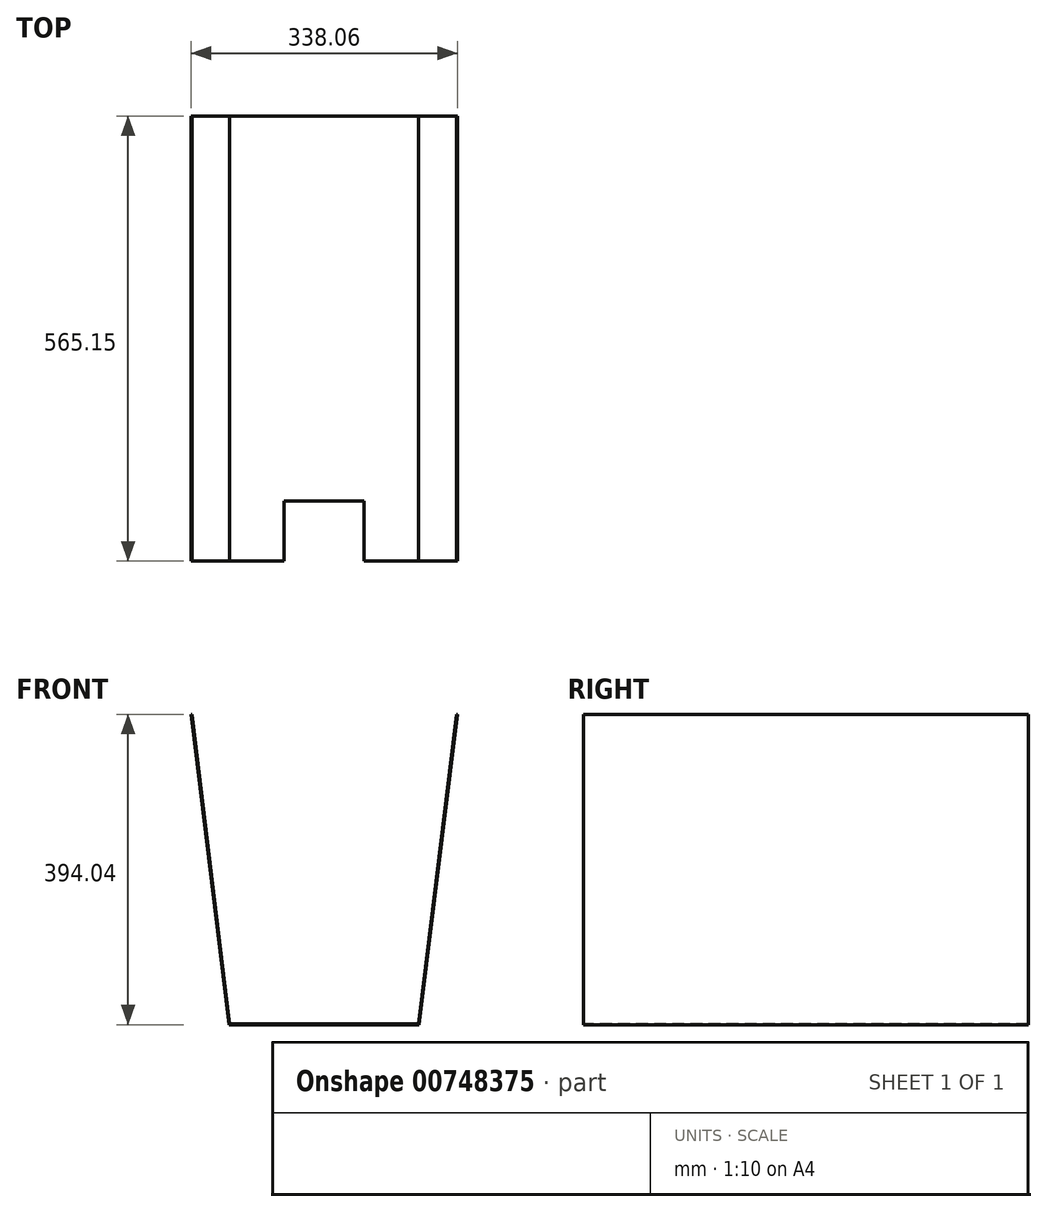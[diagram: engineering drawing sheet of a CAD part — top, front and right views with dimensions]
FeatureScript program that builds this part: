
annotation { "Feature Type Name" : "Feature", "Feature Type Description" : "" }
export const myFeature = defineFeature(function(context is Context, id is Id, definition is map)
    precondition{}
    {
        {
            var Q0;
            Q0=qCreatedBy(makeId("Front.planeOp"),FACE);
            var sketch = newSketch(context, id + "F0", { "sketchPlane" : qUnion([Q0])});
            skLineSegment(sketch, "E0", {"start": v(0, 0) * mm, "end": v(-120.65, 0) * mm});
            skLineSegment(sketch, "E1", {"start": v(-120.65, 0) * mm, "end": v(-169.03, 394.04) * mm});
            skLineSegment(sketch, "E2.MirrorCS", {"start": v(120.65, 0) * mm, "end": v(169.03, 394.04) * mm});
            skLineSegment(sketch, "E3.MirrorCS", {"start": v(0, 0) * mm, "end": v(120.65, 0) * mm});
            skLineSegment(sketch, "E4", {"start": v(-169.03, 394.04) * mm, "end": v(169.03, 394.04) * mm});
            skSolve(sketch);
        }
        {
            var Q0;
            Q0=makeQuery(id+"F0.imprint","IMPRINT",FACE,{"disambiguationData":[TD([[makeQuery(id+"F0.imprint","IMPRINT",EDGE,{"derivedFrom":sQuery(id+"F0.wireOp",EDGE,"E0")}),-1.0]])]});
            extrude(context, id + "F1", {"entities" : qUnion([Q0]), "depth" : -565.15 * mm, "offsetDistance" : 25.4 * mm});
        }
        {
            var Q0;
            Q0=makeQuery(id+"F1.opExtrude","CAP_FACE",FACE,{"disambiguationData":[OSD([sQuery(id+"F0.wireOp",EDGE,"E0"),sQuery(id+"F0.wireOp",EDGE,"E1"),sQuery(id+"F0.wireOp",EDGE,"E2.MirrorCS"),sQuery(id+"F0.wireOp",EDGE,"E3.MirrorCS"),sQuery(id+"F0.wireOp",EDGE,"E4")])],"isStart":true});
            var Q1;
            Q1=makeQuery(id+"F1.opExtrude","SWEPT_FACE",FACE,{"disambiguationData":[OSD([sQuery(id+"F0.wireOp",EDGE,"E4")])]});
            var Q2;
            Q2=makeQuery(id+"F1.opExtrude","CAP_FACE",FACE,{"disambiguationData":[OSD([sQuery(id+"F0.wireOp",EDGE,"E0"),sQuery(id+"F0.wireOp",EDGE,"E1"),sQuery(id+"F0.wireOp",EDGE,"E2.MirrorCS"),sQuery(id+"F0.wireOp",EDGE,"E3.MirrorCS"),sQuery(id+"F0.wireOp",EDGE,"E4")])],"isStart":false});
            shell(context, id + "F2", {"entities" : qUnion([Q0, Q1, Q2]), "thickness" : 0.76 * mm});
        }
        {
            var Q0;
            Q0=qCreatedBy(makeId("Top.planeOp"),FACE);
            var sketch = newSketch(context, id + "F3", { "sketchPlane" : qUnion([Q0])});
            skLineSegment(sketch, "E5.bottom", {"start": v(50.8, 0) * mm, "end": v(-50.8, 0) * mm});
            skLineSegment(sketch, "E5.top", {"start": v(50.8, 76.2) * mm, "end": v(-50.8, 76.2) * mm});
            skLineSegment(sketch, "E5.left", {"start": v(50.8, 0) * mm, "end": v(50.8, 76.2) * mm});
            skLineSegment(sketch, "E5.right", {"start": v(-50.8, 0) * mm, "end": v(-50.8, 76.2) * mm});
            skPoint(sketch, "E5.middle", {"position": v(0, 38.1) * mm});
            skSolve(sketch);
        }
        {
            var Q0;
            Q0=makeQuery(id+"F3.imprint","IMPRINT",FACE,{"disambiguationData":[TD([[makeQuery(id+"F3.imprint","IMPRINT",EDGE,{"derivedFrom":sQuery(id+"F3.wireOp",EDGE,"E5.bottom")}),-1.0]])]});
            var Q1;
            Q1=sQuery(id+"F3.wireOp",EDGE,"E5.top");
            var Q2;
            Q2=sQuery(id+"F3.wireOp",EDGE,"E5.right");
            var Q3;
            Q3=sQuery(id+"F3.wireOp",EDGE,"E5.bottom");
            var Q4;
            Q4=sQuery(id+"F3.wireOp",EDGE,"E5.left");
            extrude(context, id + "F4", {"entities" : qUnion([Q0]), "operationType" : NewBodyOperationType.REMOVE, "surfaceOperationType" : NewSurfaceOperationType.ADD, "surfaceEntities" : qUnion([Q1, Q2, Q3, Q4]), "oppositeDirection" : true, "depth" : 81.28 * mm, "offsetDistance" : 25.4 * mm, "hasSecondDirection" : true, "secondDirectionOppositeDirection" : false, "secondDirectionDepth" : 106.68 * mm});
        }
    });
